# Revit family: 1176xxx Zeppo Ceiling (UL)
name_source: partatom
category: Lighting Fixtures
units: mm (PartAtom-declared; Revit-internal decimal feet)

## family parameters
Always vertical = Yes
Cut with Voids When Loaded = No
Host = Ceiling
Light Source = No
Maintain Annotation Orientation = No
OmniClass Number = 23.80.70.11
OmniClass Title = Luminaries for Internal Lighting
Part Type = Normal
Room Calculation Point = No
Round Connector Dimension = Use Diameter
Shared = No

## types (2) — shared parameters
ADA compliant = No
Dimmable = Yes
Dimming Method = Lamp Dependent
Driver Included = Not Applicable
Driver Required = No
Efficacy (lm/w) = Lamp Dependent
Electrical Class = 1
Lamp = Incandescent
Light Source Fixed = Yes
Location / IP Rating = Damp
Main Material = Metal - Mild Steel
Manufacturer URL - Europe and Rest of World = www.astrolighting.com
Manufacturer URL - North America = us.astrolighting.com
Power (Watts) = Lamp Dependent
Product CCT = Lamp Dependent
Product CRI = Lamp Dependent
Product Dimensions (in) = 9.25x11.81
Product Location = Bathroom
Product Name = Zeppo Ceiling
Product URL = https://us.astrolighting.com
Product Weight (lb) = 4 mm  [stored 0.0131234 ft]
zero-valued in all types: Default Elevation

## per-type parameters (varying)
| type | Main Finish | Product SKU |
| 1176005 Zeppo Ceiling - Polished Chrome | Polished Chrome | 1176005 |
| 1176018 Zeppo Ceiling - Matt Black | Matt Black | 1176018 |

note: [stored X ft] marks values corroborated as IEEE doubles in the binary element streams (Revit-internal decimal feet)

## geometry (parser evidence)
native form markers: Sweep x3
no freeform markers — native parametric forms only
